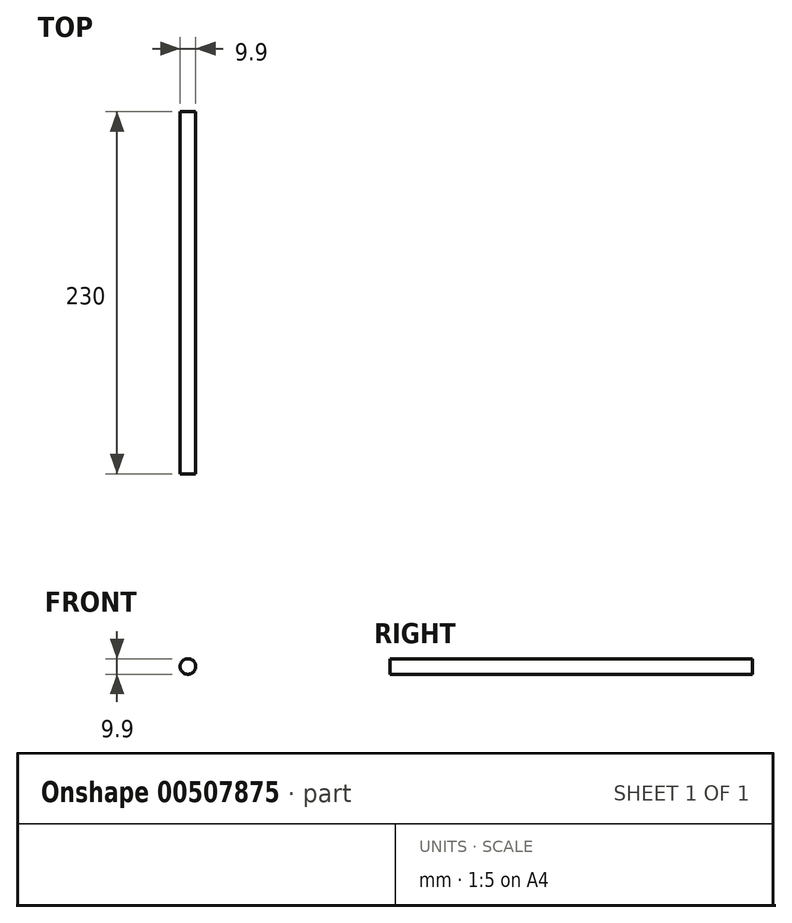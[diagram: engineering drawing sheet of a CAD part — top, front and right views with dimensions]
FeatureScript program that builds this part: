
annotation { "Feature Type Name" : "Feature", "Feature Type Description" : "" }
export const myFeature = defineFeature(function(context is Context, id is Id, definition is map)
    precondition{}
    {
        {
            var Q0;
            Q0=qCreatedBy(makeId("Front.planeOp"),FACE);
            var sketch = newSketch(context, id + "F0", { "sketchPlane" : qUnion([Q0])});
            skCircle(sketch, "E0", {"center": v(0, 0) * mm, "radius": 4.95 * mm});
            skSolve(sketch);
        }
        {
            var Q0;
            Q0=makeQuery(id+"F0.imprint","IMPRINT",FACE,{"disambiguationData":[TD([[makeQuery(id+"F0.imprint","IMPRINT",EDGE,{"derivedFrom":sQuery(id+"F0.wireOp",EDGE,"E0")}),1.0]])]});
            var Q1;
            Q1=sQuery(id+"F0.wireOp",EDGE,"E0");
            extrude(context, id + "F1", {"entities" : qUnion([Q0]), "surfaceEntities" : qUnion([Q1]), "depth" : 230 * mm});
        }
    });
